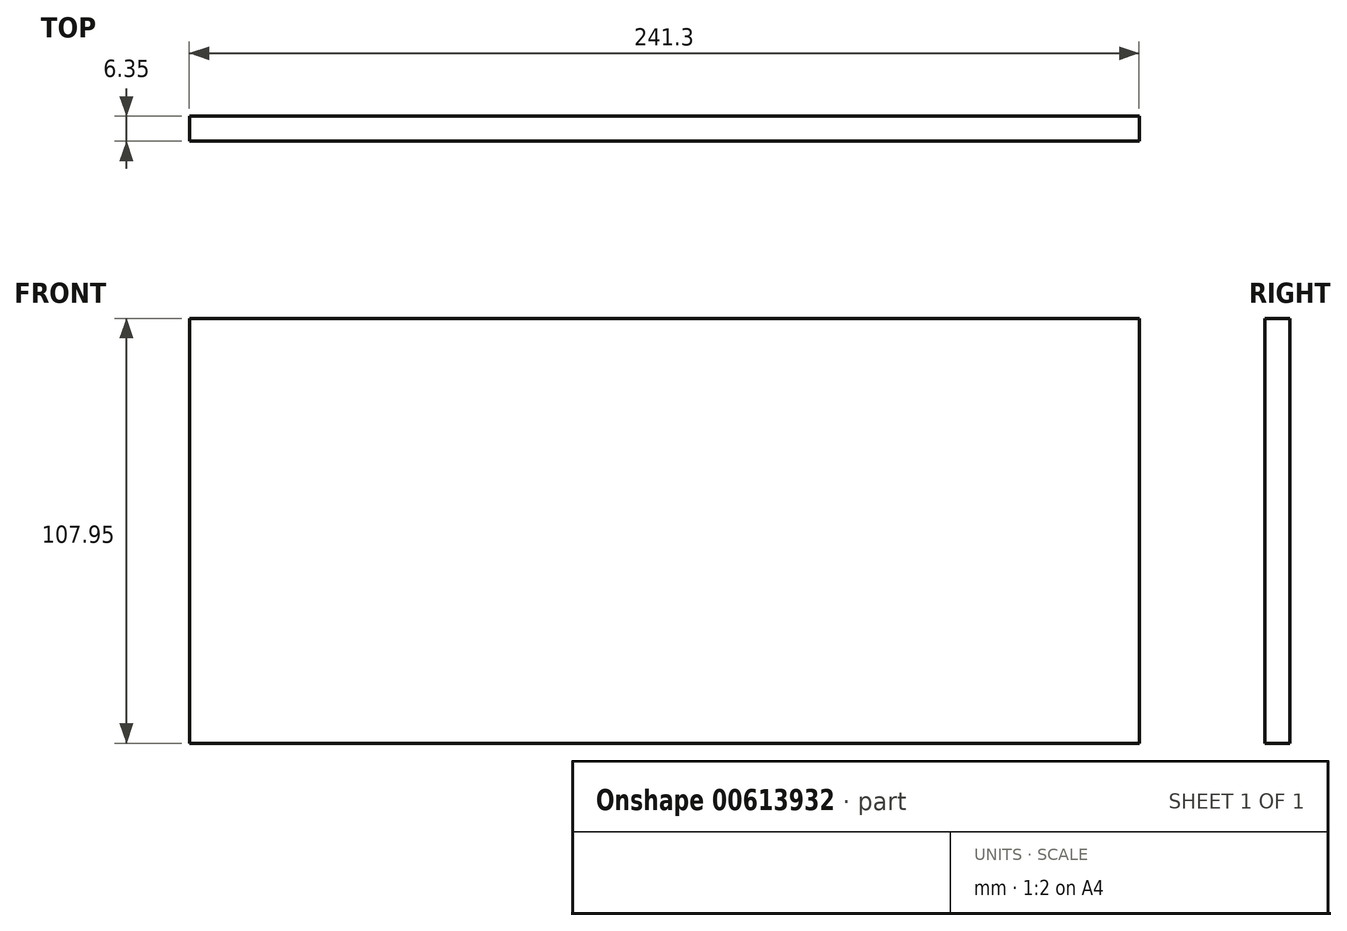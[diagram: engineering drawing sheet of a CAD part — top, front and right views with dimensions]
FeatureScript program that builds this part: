
annotation { "Feature Type Name" : "Feature", "Feature Type Description" : "" }
export const myFeature = defineFeature(function(context is Context, id is Id, definition is map)
    precondition{}
    {
        {
            var Q0;
            Q0=qCreatedBy(makeId("Top.planeOp"),FACE);
            var sketch = newSketch(context, id + "F0", { "sketchPlane" : qUnion([Q0])});
            skLineSegment(sketch, "E0.bottom", {"start": v(-101.37, 15.2) * mm, "end": v(139.93, 15.2) * mm});
            skLineSegment(sketch, "E0.top", {"start": v(-101.37, 8.86) * mm, "end": v(139.93, 8.86) * mm});
            skLineSegment(sketch, "E0.left", {"start": v(-101.37, 15.2) * mm, "end": v(-101.37, 8.86) * mm});
            skLineSegment(sketch, "E0.right", {"start": v(139.93, 15.2) * mm, "end": v(139.93, 8.86) * mm});
            skSolve(sketch);
        }
        {
            var Q0;
            Q0 = qSketchRegion(id + "F0", true);
            extrude(context, id + "F1", {"entities" : qUnion([Q0]), "depth" : 107.95 * mm, "offsetDistance" : 25.4 * mm});
        }
    });
